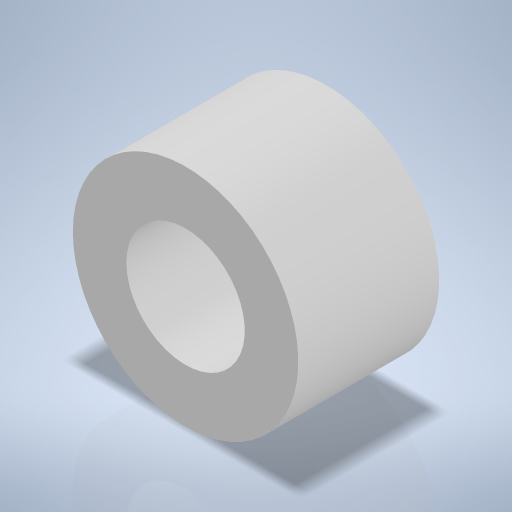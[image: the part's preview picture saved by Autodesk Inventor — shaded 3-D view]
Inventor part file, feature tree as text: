
AUTODESK INVENTOR PART (.ipt)
format: ipt  version: 2024 (Build 280153000, 153)  size: 212,480 bytes
history: native  units: mm
features: extrude x1, sketch x1
ambient origin geometry x8: Origin, YZ Plane, XZ Plane, XY Plane, X Axis, Y Axis, Z Axis, Center Point
bodies: Volumenkörper1 (feature_tree)
feature tree (2):
  extrude  "Extrusion1"  Depth=5.0mm
  sketch  "Skizze1"  dims[d0=8.0mm d1=4.2mm d2=5.0mm d3=0.0mm]
